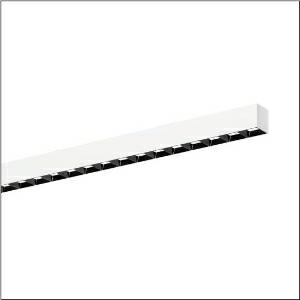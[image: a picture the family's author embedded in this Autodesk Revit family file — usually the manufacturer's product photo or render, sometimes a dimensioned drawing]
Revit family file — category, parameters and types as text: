
# Revit family: silica_r__21_51mx24tbt5w_c5f4
name_source: partatom
category: Lighting Fixtures
units: mm (PartAtom-declared; Revit-internal decimal feet)

## family parameters
Cut with Voids When Loaded = No
Host = Face
Light Source = No
Part Type = Normal
Room Calculation Point = No
Round Connector Dimension = Use Diameter
Shared = No

## types (1)
- --- (1 x LED, 4100 lm, 40.5 W, 6500K)
    Apparent Load = 41 VA
    CIE Flux Codes = 74 94 99 100 100
    Color Rendering = 80
    Color Temperature = 6500K
    Default Elevation = 1800 mm
    Description = Silica® 21, office luminaire, primary light control with darklight reflector, of PMMA, black, light emission: direct distribution, primary light characteristic: asymmetric, installation type: surface-mounted, LED, rated luminous flux: 4.100lm, luminous efficacy: 96lm/W, light colour: 8tw, colour temperature: 2700..6500K, control gear: DALI DT8, with terminal, 3+2-pole, max. 2.5mm², mains connection: 220..240V, AC, 50/60Hz, rated input power: 42.6W, luminaire housing, of aluminium, traffic white (RAL 9016), length: 1.504mm, width: 53mm, height: 53mm, protection rating (complete): IP20, insulation class (complete): insulation class I (protective earthing), certification: CE, permissible operating ambient temperature: 0..+35°C, standard: EN 50419, packaging unit: 1 piece
    Height = 53 mm
    Lamp = 1 x LED
    Lamp Light Flux = 4100 lm
    Lamp Power = 40.5 W
    Lamp count = 1
    Length = 1504 mm
    Luminous efficacy = 101 lm/W
    Manufacturer = Siteco
    ModVariant = No
    Model = 51MX24TBT5W
    Mounting Place = Ceiling
    Mounting Type = Surface mounted
    Number of Poles = 1
    OnlyDefault = Yes
    Power Factor = 1
    Product Name = Silica® 21
    Product group = office luminaire | ceiling mounted
    ProductGroupID = 302
    Protection Class = Protection class I
    Protection Degree = IP 20
    RLX_Detail_Level = 1
    RLX_Emergency_Light_Flux = 0 lm
    RLX_Emergency_Type = 0
    RLX_Emergency_Type_DB = No
    RlxData = <blob elided: 41853 chars, md5=6acc15c4>
    Socket = socket
    Standby Power = 0 W
    System Light Flux = 4100 lm
    System Power = 41 W
    Type Comments = individual setting
    Type Image = l_1335873.jpg
    URL = http://relux.com
    VarID = @adj_140010
    Voltage = 0 V
    Weight = 0.00 kg
    Width = 53 mm

## geometry (parser evidence)
native form markers: Blend x4, Sweep x10
no freeform markers — native parametric forms only
